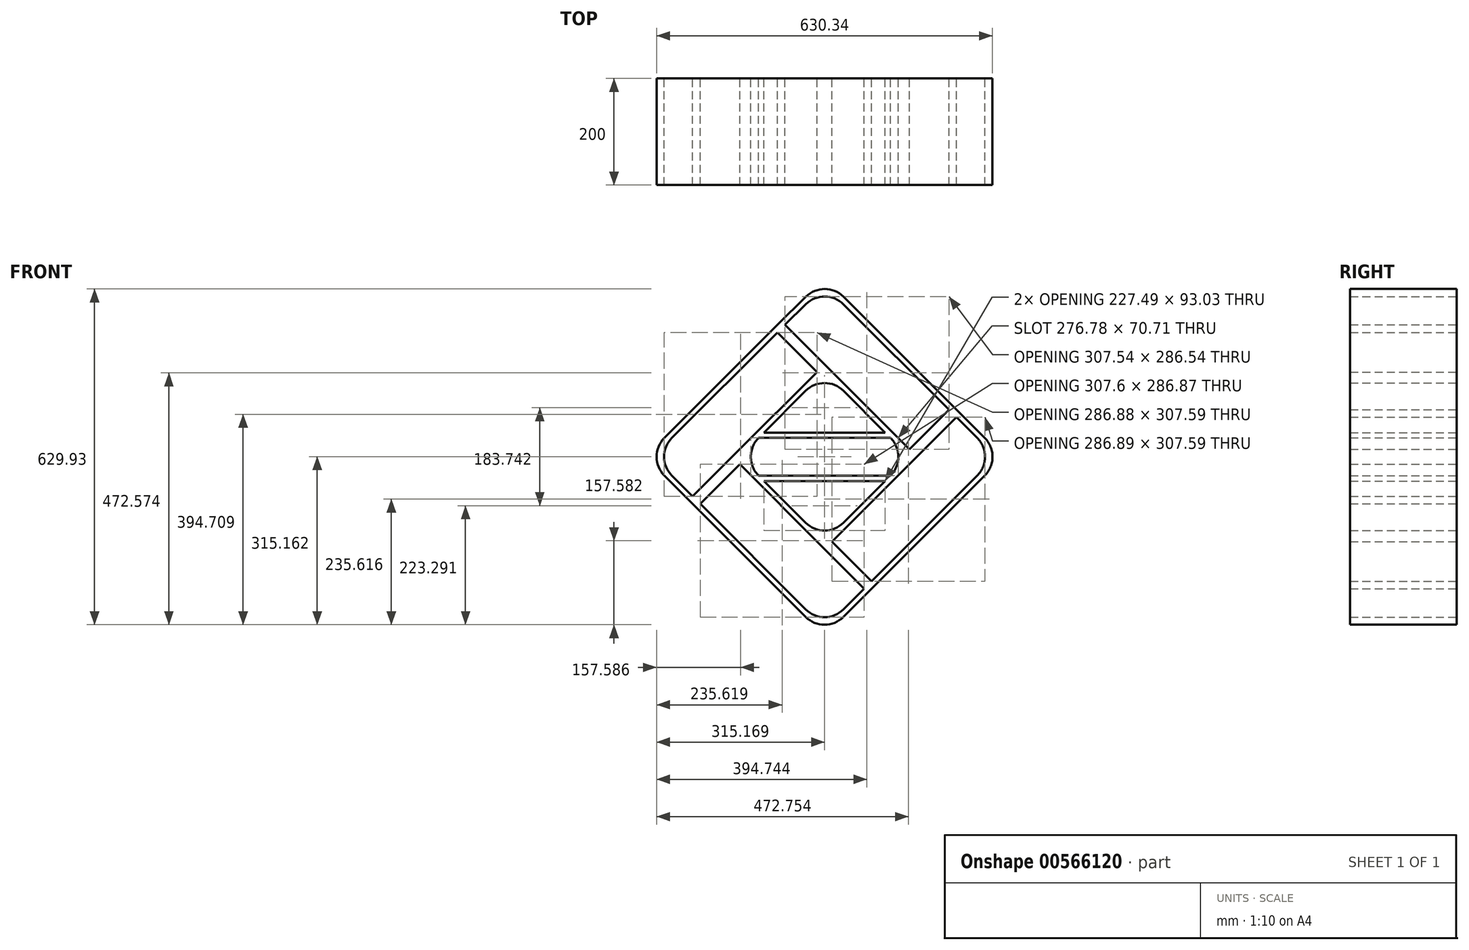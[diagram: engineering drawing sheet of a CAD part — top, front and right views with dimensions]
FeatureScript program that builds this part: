
annotation { "Feature Type Name" : "Feature", "Feature Type Description" : "" }
export const myFeature = defineFeature(function(context is Context, id is Id, definition is map)
    precondition{}
    {
        {
            var Q0;
            Q0=qCreatedBy(makeId("Front.planeOp"),FACE);
            var sketch = newSketch(context, id + "F0", { "sketchPlane" : qUnion([Q0])});
            skLineSegment(sketch, "E0", {"start": v(123.1, 36) * mm, "end": v(34.71, 124.4) * mm});
            skLineSegment(sketch, "E1", {"start": v(34.71, -123.1) * mm, "end": v(123.1, -34.7) * mm});
            skLineSegment(sketch, "E2", {"start": v(-124.39, 36) * mm, "end": v(-36, 124.4) * mm});
            skLineSegment(sketch, "E3", {"start": v(-124.39, -34.7) * mm, "end": v(-36, -123.1) * mm});
            skLineSegment(sketch, "E4", {"start": v(158.46, 0.65) * mm, "end": v(246.85, 89.04) * mm});
            skLineSegment(sketch, "E5", {"start": v(246.85, 89.04) * mm, "end": v(35.1, 300.78) * mm});
            skLineSegment(sketch, "E6", {"start": v(-35.35, 301.04) * mm, "end": v(-89.03, 248.14) * mm});
            skLineSegment(sketch, "E7", {"start": v(-89.03, 248.14) * mm, "end": v(-0.64, 159.75) * mm});
            skLineSegment(sketch, "E8", {"start": v(-89.03, 248.14) * mm, "end": v(-301.16, 36) * mm});
            skLineSegment(sketch, "E9", {"start": v(-301.16, -34.7) * mm, "end": v(-248.13, -87.74) * mm});
            skLineSegment(sketch, "E10", {"start": v(-248.13, -87.74) * mm, "end": v(-159.74, 0.65) * mm});
            skLineSegment(sketch, "E11", {"start": v(-248.13, -87.74) * mm, "end": v(-36, -299.86) * mm});
            skLineSegment(sketch, "E12", {"start": v(34.71, -299.86) * mm, "end": v(87.75, -246.83) * mm});
            skLineSegment(sketch, "E13", {"start": v(87.75, -246.83) * mm, "end": v(-0.64, -158.44) * mm});
            skLineSegment(sketch, "E14", {"start": v(87.75, -246.83) * mm, "end": v(299.88, -34.7) * mm});
            skLineSegment(sketch, "E15", {"start": v(299.88, 36) * mm, "end": v(246.85, 89.04) * mm});
            skLineSegment(sketch, "E16.0", {"start": v(-35.4, 286.95) * mm, "end": v(-74.84, 248.08) * mm});
            skLineSegment(sketch, "E16.1", {"start": v(232.7, 89.04) * mm, "end": v(35.05, 286.7) * mm});
            skLineSegment(sketch, "E16.2", {"start": v(-74.84, 248.08) * mm, "end": v(6.43, 166.82) * mm});
            skLineSegment(sketch, "E16.3", {"start": v(158.46, 14.8) * mm, "end": v(6.43, 166.82) * mm});
            skLineSegment(sketch, "E16.4", {"start": v(158.46, 14.8) * mm, "end": v(232.7, 89.04) * mm});
            skLineSegment(sketch, "E17.0", {"start": v(285.74, 36) * mm, "end": v(246.85, 74.9) * mm});
            skLineSegment(sketch, "E17.1", {"start": v(87.75, -232.69) * mm, "end": v(285.74, -34.7) * mm});
            skLineSegment(sketch, "E17.2", {"start": v(165.53, -6.42) * mm, "end": v(246.85, 74.9) * mm});
            skLineSegment(sketch, "E17.3", {"start": v(13.5, -158.44) * mm, "end": v(165.53, -6.42) * mm});
            skLineSegment(sketch, "E17.4", {"start": v(87.75, -232.69) * mm, "end": v(13.5, -158.44) * mm});
            skLineSegment(sketch, "E18.0", {"start": v(34.71, -285.72) * mm, "end": v(73.6, -246.83) * mm});
            skLineSegment(sketch, "E18.1", {"start": v(-233.99, -87.74) * mm, "end": v(-36, -285.72) * mm});
            skLineSegment(sketch, "E18.2", {"start": v(73.6, -246.83) * mm, "end": v(-7.71, -165.51) * mm});
            skLineSegment(sketch, "E18.3", {"start": v(-159.74, -13.5) * mm, "end": v(-7.71, -165.51) * mm});
            skLineSegment(sketch, "E18.4", {"start": v(-233.99, -87.74) * mm, "end": v(-159.74, -13.5) * mm});
            skLineSegment(sketch, "E19.0", {"start": v(-248.13, -73.6) * mm, "end": v(-166.82, 7.72) * mm});
            skLineSegment(sketch, "E19.1", {"start": v(-287.02, -34.7) * mm, "end": v(-248.13, -73.6) * mm});
            skLineSegment(sketch, "E19.2", {"start": v(-166.82, 7.72) * mm, "end": v(-14.78, 159.75) * mm});
            skLineSegment(sketch, "E19.3", {"start": v(-89.03, 234) * mm, "end": v(-14.78, 159.75) * mm});
            skLineSegment(sketch, "E19.4", {"start": v(-89.03, 234) * mm, "end": v(-287.02, 36) * mm});
            skLineSegment(sketch, "E20", {"start": v(0, 335.88) * mm, "end": v(-236.52, 335.88) * mm});
            skLineSegment(sketch, "E21", {"start": v(-336.52, 235.88) * mm, "end": v(-336.52, 0.65) * mm});
            skLineSegment(sketch, "E22", {"start": v(-336.52, 0.65) * mm, "end": v(-336.52, -235.22) * mm});
            skLineSegment(sketch, "E23", {"start": v(-236.52, -335.22) * mm, "end": v(-0.64, -335.22) * mm});
            skLineSegment(sketch, "E24", {"start": v(-0.64, -335.22) * mm, "end": v(235.24, -335.22) * mm});
            skLineSegment(sketch, "E25", {"start": v(335.24, -235.22) * mm, "end": v(335.24, 0.65) * mm});
            skLineSegment(sketch, "E26", {"start": v(0, 335.88) * mm, "end": v(235.24, 335.88) * mm});
            skLineSegment(sketch, "E27", {"start": v(335.24, 235.88) * mm, "end": v(335.24, 0.65) * mm});
            skPoint(sketch, "E28.visualSharp", {"position": v(-336.52, 335.88) * mm});
            skArc(sketch, "E28.filletArc", {"start": v(-236.52, 335.88) * mm, "mid": v(-307.23, 306.59) * mm, "end": v(-336.52, 235.88) * mm});
            skPoint(sketch, "E29.visualSharp", {"position": v(335.24, 335.88) * mm});
            skArc(sketch, "E29.filletArc", {"start": v(335.24, 235.88) * mm, "mid": v(305.95, 306.59) * mm, "end": v(235.24, 335.88) * mm});
            skPoint(sketch, "E30.visualSharp", {"position": v(335.24, -335.22) * mm});
            skArc(sketch, "E30.filletArc", {"start": v(235.24, -335.22) * mm, "mid": v(305.95, -305.93) * mm, "end": v(335.24, -235.22) * mm});
            skPoint(sketch, "E31.visualSharp", {"position": v(-336.52, -335.22) * mm});
            skArc(sketch, "E31.filletArc", {"start": v(-336.52, -235.22) * mm, "mid": v(-307.23, -305.93) * mm, "end": v(-236.52, -335.22) * mm});
            skCircle(sketch, "E32", {"center": v(235.24, -235.22) * mm, "radius": 50 * mm});
            skCircle(sketch, "E33", {"center": v(-236.52, -235.22) * mm, "radius": 50 * mm});
            skCircle(sketch, "E34", {"center": v(-236.52, 235.88) * mm, "radius": 65 * mm});
            skCircle(sketch, "E35", {"center": v(235.24, 235.88) * mm, "radius": 65 * mm});
            skPoint(sketch, "E36.visualSharp", {"position": v(0, 335.88) * mm});
            skArc(sketch, "E36.filletArc", {"start": v(35.1, 300.78) * mm, "mid": v(-0.07, 315.42) * mm, "end": v(-35.35, 301.04) * mm});
            skPoint(sketch, "E37.visualSharp", {"position": v(-0.05, 321.79) * mm});
            skArc(sketch, "E37.filletArc", {"start": v(35.05, 286.7) * mm, "mid": v(-0.13, 301.33) * mm, "end": v(-35.4, 286.95) * mm});
            skPoint(sketch, "E38.visualSharp", {"position": v(335.24, 0.65) * mm});
            skArc(sketch, "E38.filletArc", {"start": v(299.88, -34.7) * mm, "mid": v(314.53, 0.65) * mm, "end": v(299.88, 36) * mm});
            skPoint(sketch, "E39.visualSharp", {"position": v(321.1, 0.65) * mm});
            skArc(sketch, "E39.filletArc", {"start": v(285.74, -34.7) * mm, "mid": v(300.39, 0.65) * mm, "end": v(285.74, 36) * mm});
            skPoint(sketch, "E40.visualSharp", {"position": v(-0.64, -321.07) * mm});
            skArc(sketch, "E40.filletArc", {"start": v(-36, -285.72) * mm, "mid": v(-0.64, -300.36) * mm, "end": v(34.71, -285.72) * mm});
            skPoint(sketch, "E41.visualSharp", {"position": v(-0.64, -335.22) * mm});
            skArc(sketch, "E41.filletArc", {"start": v(-36, -299.86) * mm, "mid": v(-0.64, -314.5) * mm, "end": v(34.71, -299.86) * mm});
            skPoint(sketch, "E42.visualSharp", {"position": v(-336.52, 0.65) * mm});
            skArc(sketch, "E42.filletArc", {"start": v(-301.16, 36) * mm, "mid": v(-315.8, 0.65) * mm, "end": v(-301.16, -34.7) * mm});
            skPoint(sketch, "E43.visualSharp", {"position": v(-322.37, 0.65) * mm});
            skArc(sketch, "E43.filletArc", {"start": v(-287.02, 36) * mm, "mid": v(-301.66, 0.65) * mm, "end": v(-287.02, -34.7) * mm});
            skPoint(sketch, "E44.visualSharp", {"position": v(-0.64, 159.75) * mm});
            skArc(sketch, "E44.filletArc", {"start": v(34.71, 124.4) * mm, "mid": v(-0.64, 139.04) * mm, "end": v(-36, 124.4) * mm});
            skPoint(sketch, "E45.visualSharp", {"position": v(-159.74, 0.65) * mm});
            skArc(sketch, "E45.filletArc", {"start": v(-124.39, 36) * mm, "mid": v(-139.03, 0.65) * mm, "end": v(-124.39, -34.7) * mm});
            skPoint(sketch, "E46.visualSharp", {"position": v(-0.64, -158.44) * mm});
            skArc(sketch, "E46.filletArc", {"start": v(-36, -123.1) * mm, "mid": v(-0.64, -137.73) * mm, "end": v(34.71, -123.1) * mm});
            skPoint(sketch, "E47.visualSharp", {"position": v(158.46, 0.65) * mm});
            skArc(sketch, "E47.filletArc", {"start": v(123.1, -34.7) * mm, "mid": v(137.75, 0.65) * mm, "end": v(123.1, 36) * mm});
            skLineSegment(sketch, "E48", {"start": v(-166.82, 7.72) * mm, "end": v(-241.06, 81.97) * mm});
            skCircle(sketch, "E49", {"center": v(-59.3, 0) * mm, "radius": 14.15 * mm});
            skCircle(sketch, "E50", {"center": v(19.77, 0) * mm, "radius": 14.15 * mm});
            skCircle(sketch, "E51", {"center": v(59.3, 0) * mm, "radius": 14.15 * mm});
            skCircle(sketch, "E52", {"center": v(-19.77, 0) * mm, "radius": 14.15 * mm});
            skLineSegment(sketch, "E53", {"start": v(-124.39, -34.7) * mm, "end": v(123.1, -34.7) * mm});
            skLineSegment(sketch, "E54", {"start": v(-124.39, 36) * mm, "end": v(123.1, 36) * mm});
            skLineSegment(sketch, "E55.0", {"start": v(-114.39, 46) * mm, "end": v(113.1, 46) * mm});
            skLineSegment(sketch, "E56.0", {"start": v(-114.39, -44.7) * mm, "end": v(113.1, -44.7) * mm});
            skSolve(sketch);
        }
        {
            var Q0;
            Q0=makeQuery(id+"F0.imprint","IMPRINT",FACE,{"disambiguationData":[TD([[makeQuery(id+"F0.imprint","IMPRINT",EDGE,{"derivedFrom":sQuery(id+"F0.wireOp",EDGE,"E2")}),1.0]])]});
            var Q1;
            Q1=makeQuery(id+"F0.imprint","IMPRINT",FACE,{"disambiguationData":[TD([[makeQuery(id+"F0.imprint","IMPRINT",EDGE,{"derivedFrom":sQuery(id+"F0.wireOp",EDGE,"E0")}),-1.0]])]});
            var Q2;
            Q2=makeQuery(id+"F0.imprint","IMPRINT",FACE,{"disambiguationData":[TD([[makeQuery(id+"F0.imprint","IMPRINT",EDGE,{"derivedFrom":sQuery(id+"F0.wireOp",EDGE,"E1")}),-1.0]])]});
            var Q3;
            Q3=makeQuery(id+"F0.imprint","IMPRINT",FACE,{"disambiguationData":[TD([[makeQuery(id+"F0.imprint","IMPRINT",EDGE,{"derivedFrom":sQuery(id+"F0.wireOp",EDGE,"E3")}),-1.0]])]});
            extrude(context, id + "F1", {"entities" : qUnion([Q0, Q1, Q2, Q3]), "depth" : 200 * mm, "offsetDistance" : 25 * mm});
        }
        {
            var Q0;
            {var subQ0=sQuery(id+"F0.wireOp",EDGE,"E54");Q0=makeQuery(id+"F0.imprint","IMPRINT",FACE,{"disambiguationData":[TD([[makeQuery(id+"F0.imprint","IMPRINT",EDGE,{"derivedFrom":subQ0}),1.0]])]});}
            var Q1;
            {var subQ0=sQuery(id+"F0.wireOp",EDGE,"E53");Q1=makeQuery(id+"F0.imprint","IMPRINT",FACE,{"disambiguationData":[TD([[makeQuery(id+"F0.imprint","IMPRINT",EDGE,{"derivedFrom":subQ0}),-1.0]])]});}
            extrude(context, id + "F2", {"entities" : qUnion([Q0, Q1]), "operationType" : NewBodyOperationType.ADD, "depth" : 200 * mm, "offsetDistance" : 25 * mm});
        }
    });
